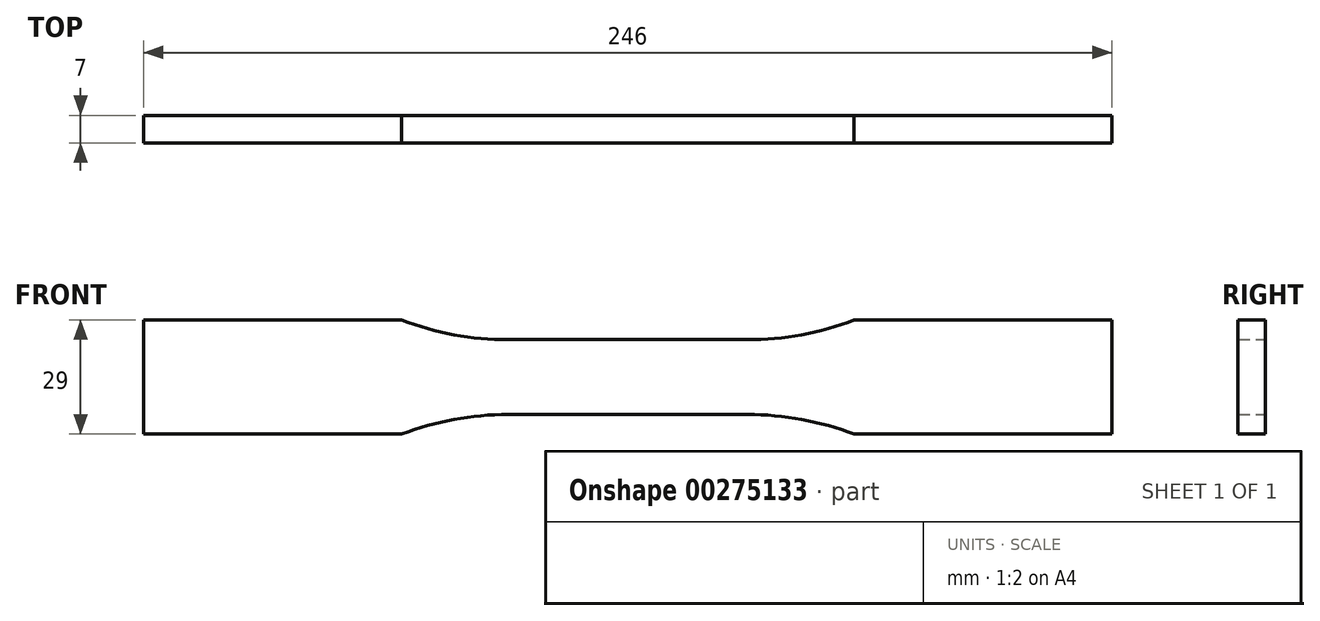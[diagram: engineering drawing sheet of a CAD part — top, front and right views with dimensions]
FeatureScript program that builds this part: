
annotation { "Feature Type Name" : "Feature", "Feature Type Description" : "" }
export const myFeature = defineFeature(function(context is Context, id is Id, definition is map)
    precondition{}
    {
        {
            var Q0;
            Q0=qCreatedBy(makeId("Front.planeOp"),FACE);
            var sketch = newSketch(context, id + "F0", { "sketchPlane" : qUnion([Q0])});
            skLineSegment(sketch, "E0", {"start": v(0, 9.5) * mm, "end": v(30.39, 9.5) * mm});
            skArc(sketch, "E1", {"start": v(30.39, 9.5) * mm, "mid": v(44.17, 10.76) * mm, "end": v(57.5, 14.5) * mm});
            skLineSegment(sketch, "E2", {"start": v(57.5, 14.5) * mm, "end": v(123, 14.5) * mm});
            skLineSegment(sketch, "E3", {"start": v(123, 14.5) * mm, "end": v(123, 0) * mm});
            skLineSegment(sketch, "E4.MirrorCS", {"start": v(0, -9.5) * mm, "end": v(30.39, -9.5) * mm});
            skLineSegment(sketch, "E5.MirrorCS", {"start": v(123, -14.5) * mm, "end": v(123, 0) * mm});
            skLineSegment(sketch, "E6.MirrorCS", {"start": v(57.5, -14.5) * mm, "end": v(123, -14.5) * mm});
            skArc(sketch, "E7.MirrorCS", {"start": v(30.39, -9.5) * mm, "mid": v(44.17, -10.76) * mm, "end": v(57.5, -14.5) * mm});
            skArc(sketch, "E8.MirrorCS", {"start": v(-30.39, -9.5) * mm, "mid": v(-44.17, -10.76) * mm, "end": v(-57.5, -14.5) * mm});
            skLineSegment(sketch, "E9.MirrorCS", {"start": v(-57.5, -14.5) * mm, "end": v(-123, -14.5) * mm});
            skArc(sketch, "E10.MirrorCS", {"start": v(-30.39, 9.5) * mm, "mid": v(-44.17, 10.76) * mm, "end": v(-57.5, 14.5) * mm});
            skLineSegment(sketch, "E11.MirrorCS", {"start": v(-57.5, 14.5) * mm, "end": v(-123, 14.5) * mm});
            skLineSegment(sketch, "E12.MirrorCS", {"start": v(-123, -14.5) * mm, "end": v(-123, 0) * mm});
            skLineSegment(sketch, "E13.MirrorCS", {"start": v(0, -9.5) * mm, "end": v(-30.39, -9.5) * mm});
            skLineSegment(sketch, "E14.MirrorCS", {"start": v(-123, 14.5) * mm, "end": v(-123, 0) * mm});
            skLineSegment(sketch, "E15.MirrorCS", {"start": v(0, 9.5) * mm, "end": v(-30.39, 9.5) * mm});
            skSolve(sketch);
        }
        {
            var Q0;
            Q0 = qSketchRegion(id + "F0", true);
            extrude(context, id + "F1", {"entities" : qUnion([Q0]), "endBound" : BoundingType.SYMMETRIC, "depth" : 7 * mm});
        }
    });
